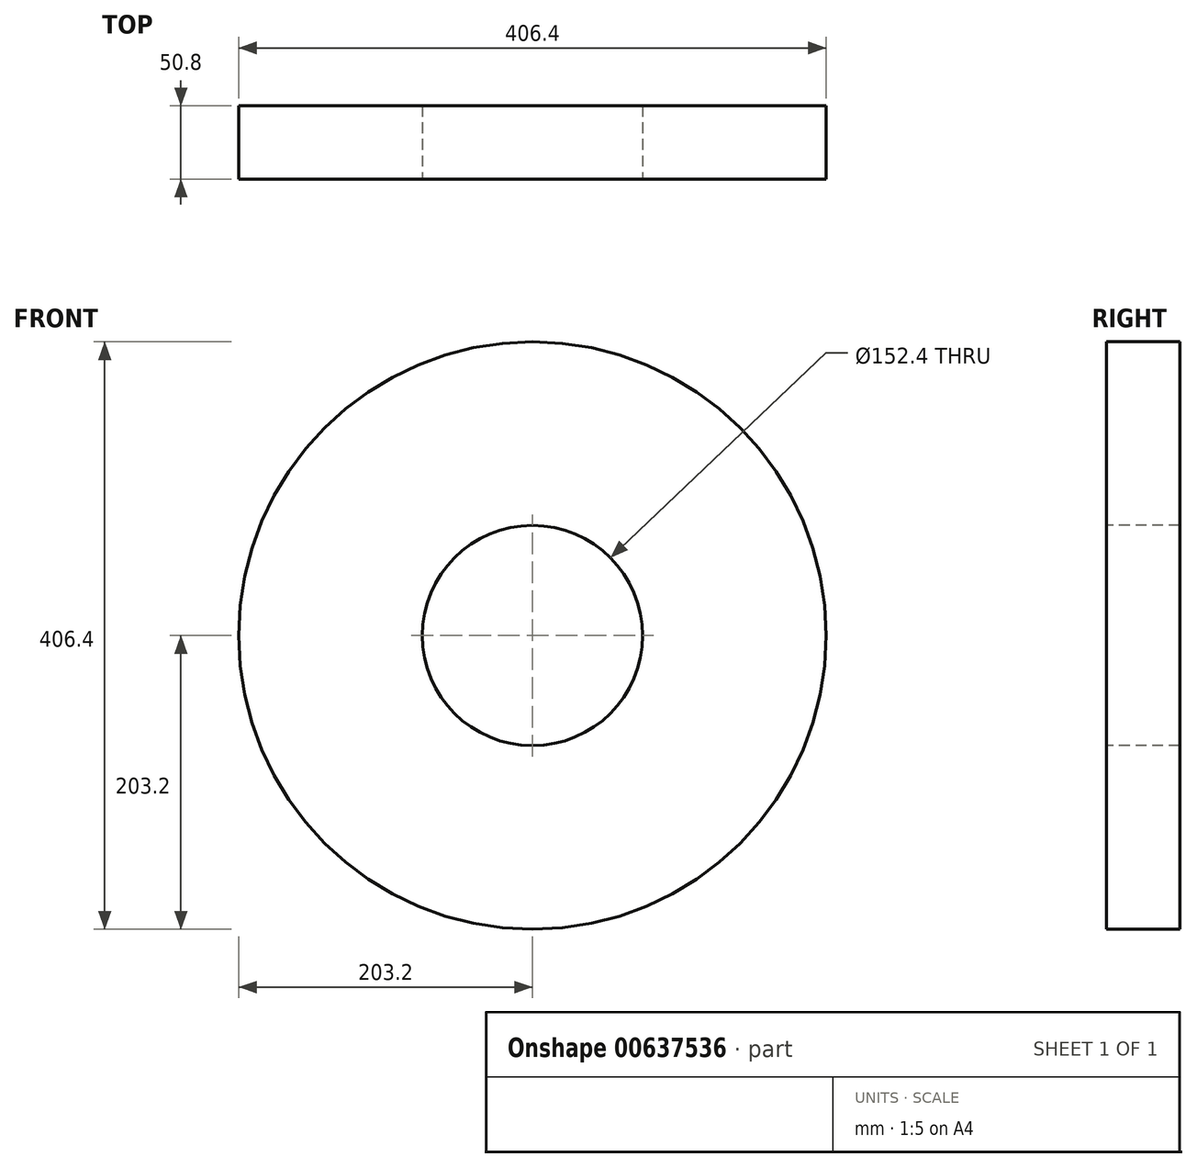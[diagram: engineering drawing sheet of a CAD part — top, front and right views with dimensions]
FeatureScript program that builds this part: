
annotation { "Feature Type Name" : "Feature", "Feature Type Description" : "" }
export const myFeature = defineFeature(function(context is Context, id is Id, definition is map)
    precondition{}
    {
        {
            var Q0;
            Q0=qCreatedBy(makeId("Top.planeOp"),FACE);
            var sketch = newSketch(context, id + "F0", { "sketchPlane" : qUnion([Q0])});
            skLineSegment(sketch, "E0.bottom", {"start": v(76.2, 0) * mm, "end": v(203.2, 0) * mm});
            skLineSegment(sketch, "E0.top", {"start": v(76.2, 50.8) * mm, "end": v(203.2, 50.8) * mm});
            skLineSegment(sketch, "E0.left", {"start": v(76.2, 0) * mm, "end": v(76.2, 50.8) * mm});
            skLineSegment(sketch, "E0.right", {"start": v(203.2, 0) * mm, "end": v(203.2, 50.8) * mm});
            skLineSegment(sketch, "E1", {"start": v(0, 0) * mm, "end": v(0, 102.26) * mm, "construction": true});
            skSolve(sketch);
        }
        {
            var Q0;
            Q0=makeQuery(id+"F0.imprint","IMPRINT",FACE,{"disambiguationData":[TD([[makeQuery(id+"F0.imprint","IMPRINT",EDGE,{"derivedFrom":sQuery(id+"F0.wireOp",EDGE,"E0.bottom")}),1.0]])]});
            var Q1;
            Q1=sQuery(id+"F0.wireOp",EDGE,"E1");
            revolve(context, id + "F1", {"entities" : qUnion([Q0]), "axis" : qUnion([Q1]), "revolveType" : RevolveType.FULL});
        }
    });
